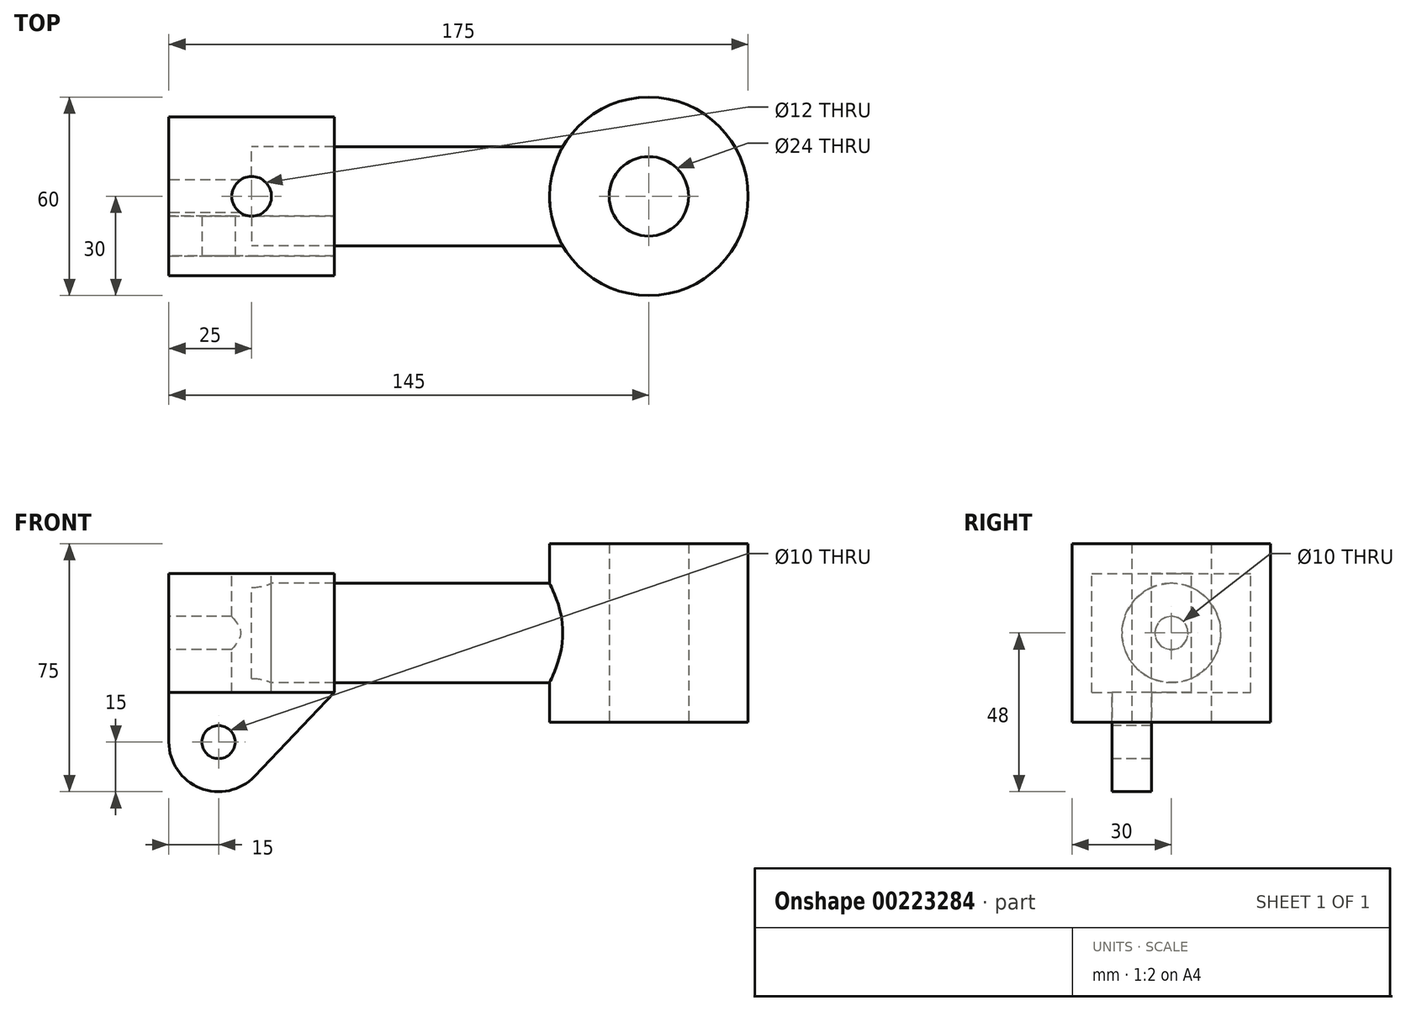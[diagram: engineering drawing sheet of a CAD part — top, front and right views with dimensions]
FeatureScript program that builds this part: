
annotation { "Feature Type Name" : "Feature", "Feature Type Description" : "" }
export const myFeature = defineFeature(function(context is Context, id is Id, definition is map)
    precondition{}
    {
        {
            var Q0;
            Q0=qCreatedBy(makeId("Top.planeOp"),FACE);
            var sketch = newSketch(context, id + "F0", { "sketchPlane" : qUnion([Q0])});
            skCircle(sketch, "E0", {"center": v(0, 0) * mm, "radius": 30 * mm});
            skCircle(sketch, "E1", {"center": v(0, 0) * mm, "radius": 12 * mm});
            skSolve(sketch);
        }
        {
            var Q0;
            Q0=makeQuery(id+"F0.imprint","IMPRINT",FACE,{"disambiguationData":[TD([[makeQuery(id+"F0.imprint","IMPRINT",EDGE,{"derivedFrom":sQuery(id+"F0.wireOp",EDGE,"E0")}),1.0]])]});
            extrude(context, id + "F1", {"entities" : qUnion([Q0]), "depth" : 54 * mm});
        }
        {
            var Q0;
            Q0=qCreatedBy(makeId("Front.planeOp"),FACE);
            var sketch = newSketch(context, id + "F2", { "sketchPlane" : qUnion([Q0])});
            skLineSegment(sketch, "E2.bottom", {"start": v(-95, 9) * mm, "end": v(-145, 9) * mm});
            skLineSegment(sketch, "E2.top", {"start": v(-95, 45) * mm, "end": v(-145, 45) * mm});
            skLineSegment(sketch, "E2.left", {"start": v(-95, 9) * mm, "end": v(-95, 45) * mm});
            skLineSegment(sketch, "E2.right", {"start": v(-145, 9) * mm, "end": v(-145, 45) * mm});
            skPoint(sketch, "E2.middle", {"position": v(-120, 27) * mm});
            skLineSegment(sketch, "E3", {"start": v(-225.9, 0) * mm, "end": v(58.93, 0) * mm, "construction": true});
            skSolve(sketch);
        }
        {
            var Q0;
            Q0=makeQuery(id+"F2.imprint","IMPRINT",FACE,{"disambiguationData":[TD([[makeQuery(id+"F2.imprint","IMPRINT",EDGE,{"derivedFrom":sQuery(id+"F2.wireOp",EDGE,"E2.bottom")}),-1.0]])]});
            extrude(context, id + "F3", {"entities" : qUnion([Q0]), "endBound" : BoundingType.SYMMETRIC, "depth" : 48 * mm});
        }
        {
            var Q0;
            Q0=qCreatedBy(makeId("Top.planeOp"),FACE);
            cPlane(context, id + "F4", {"entities" : qUnion([Q0]), "cplaneType" : CPlaneType.OFFSET, "offset" : 27 * mm, "width" : 150 * mm, "height" : 150 * mm});
        }
        {
            var Q0;
            Q0=qCreatedBy(id+"F4.planeOp",FACE);
            var sketch = newSketch(context, id + "F5", { "sketchPlane" : qUnion([Q0])});
            skLineSegment(sketch, "E4", {"start": v(-120, -40.5) * mm, "end": v(-120, 47.85) * mm, "construction": true});
            skLineSegment(sketch, "E5", {"start": v(0, 0) * mm, "end": v(-120, 0) * mm, "construction": true});
            skSolve(sketch);
        }
        {
            var Q0;
            Q0=qCreatedBy(id+"F4.planeOp",FACE);
            var sketch = newSketch(context, id + "F6", { "sketchPlane" : qUnion([Q0])});
            skLineSegment(sketch, "E6", {"start": v(0, 0) * mm, "end": v(0, -15) * mm});
            skLineSegment(sketch, "E7", {"start": v(0, -15) * mm, "end": v(-120, -15) * mm});
            skLineSegment(sketch, "E8", {"start": v(-120, -15) * mm, "end": v(-120, 0) * mm});
            skLineSegment(sketch, "E9", {"start": v(-120, 0) * mm, "end": v(0, 0) * mm});
            skSolve(sketch);
        }
        {
            var Q0;
            Q0=makeQuery(id+"F6.imprint","IMPRINT",FACE,{"disambiguationData":[TD([[makeQuery(id+"F6.imprint","IMPRINT",EDGE,{"derivedFrom":sQuery(id+"F6.wireOp",EDGE,"E6")}),-1.0]])]});
            var Q1;
            Q1=sQuery(id+"F6.wireOp",EDGE,"E9");
            revolve(context, id + "F7", {"entities" : qUnion([Q0]), "axis" : qUnion([Q1]), "revolveType" : RevolveType.FULL});
        }
        {
            var Q0;
            Q0=makeQuery(id+"F3.opExtrude","SWEPT_FACE",FACE,{"disambiguationData":[OSD([sQuery(id+"F2.wireOp",EDGE,"E2.top")])]});
            var sketch = newSketch(context, id + "F8", { "sketchPlane" : qUnion([Q0])});
            skCircle(sketch, "E10", {"center": v(-120, 0) * mm, "radius": 6 * mm});
            skSolve(sketch);
        }
        {
            var Q0;
            Q0=makeQuery(id+"F8.imprint","IMPRINT",FACE,{"disambiguationData":[TD([[makeQuery(id+"F8.imprint","IMPRINT",EDGE,{"derivedFrom":sQuery(id+"F8.wireOp",EDGE,"E10")}),1.0]])]});
            extrude(context, id + "F9", {"entities" : qUnion([Q0]), "operationType" : NewBodyOperationType.REMOVE, "endBound" : BoundingType.UP_TO_NEXT, "oppositeDirection" : true, "depth" : 25 * mm});
        }
        {
            var Q0;
            Q0=makeQuery(id+"F3.opExtrude","SWEPT_FACE",FACE,{"disambiguationData":[OSD([sQuery(id+"F2.wireOp",EDGE,"E2.right")])]});
            var sketch = newSketch(context, id + "F10", { "sketchPlane" : qUnion([Q0])});
            skCircle(sketch, "E11", {"center": v(0, 27) * mm, "radius": 5 * mm});
            skPoint(sketch, "E11.centerSnap0", {"position": v(-24, 27) * mm});
            skSolve(sketch);
        }
        {
            var Q0;
            Q0=makeQuery(id+"F10.imprint","IMPRINT",FACE,{"disambiguationData":[TD([[makeQuery(id+"F10.imprint","IMPRINT",EDGE,{"derivedFrom":sQuery(id+"F10.wireOp",EDGE,"E11")}),1.0]])]});
            extrude(context, id + "F11", {"entities" : qUnion([Q0]), "operationType" : NewBodyOperationType.REMOVE, "endBound" : BoundingType.UP_TO_NEXT, "oppositeDirection" : true, "depth" : 25 * mm});
        }
        {
            var Q0;
            Q0=makeQuery(id+"F3.opExtrude","CAP_FACE",FACE,{"disambiguationData":[OSD([sQuery(id+"F2.wireOp",EDGE,"E2.bottom"),sQuery(id+"F2.wireOp",EDGE,"E2.top"),sQuery(id+"F2.wireOp",EDGE,"E2.left"),sQuery(id+"F2.wireOp",EDGE,"E2.right")])],"isStart":false});
            cPlane(context, id + "F12", {"entities" : qUnion([Q0]), "cplaneType" : CPlaneType.OFFSET, "offset" : 6 * mm, "oppositeDirection" : true, "width" : 150 * mm, "height" : 150 * mm});
        }
        {
            var Q0;
            Q0=qCreatedBy(id+"F12.planeOp",FACE);
            var sketch = newSketch(context, id + "F13", { "sketchPlane" : qUnion([Q0])});
            skLineSegment(sketch, "E12.0", {"start": v(-95, 9) * mm, "end": v(-145, 9) * mm});
            skLineSegment(sketch, "E13", {"start": v(-145, 9) * mm, "end": v(-145, -6) * mm});
            skLineSegment(sketch, "E14", {"start": v(-119.14, -16.34) * mm, "end": v(-95, 9) * mm});
            skArc(sketch, "E15", {"start": v(-145, -6) * mm, "mid": v(-135.57, -19.93) * mm, "end": v(-119.14, -16.34) * mm});
            skCircle(sketch, "E16", {"center": v(-130, -6) * mm, "radius": 5 * mm});
            skSolve(sketch);
        }
        {
            var Q0;
            Q0=makeQuery(id+"F13.imprint","IMPRINT",FACE,{"disambiguationData":[TD([[makeQuery(id+"F13.imprint","IMPRINT",EDGE,{"derivedFrom":sQuery(id+"F13.wireOp",EDGE,"E12.0")}),1.0]])]});
            extrude(context, id + "F14", {"entities" : qUnion([Q0]), "operationType" : NewBodyOperationType.ADD, "oppositeDirection" : true, "depth" : 12 * mm});
        }
        {
            var Q0;
            Q0=makeQuery(id+"F1.opExtrude","SWEPT_BODY",BODY,{"disambiguationData":[OSD([sQuery(id+"F0.wireOp",EDGE,"E0"),sQuery(id+"F0.wireOp",EDGE,"E1")])]});
            var Q1;
            Q1=qCreatedBy(makeId("Front.planeOp"),FACE);
            mirror(context, id + "F15", {"operationType" : NewBodyOperationType.ADD, "entities" : qUnion([Q0]), "mirrorPlane" : qUnion([Q1])});
        }
        {
            var Q0;
            Q0=makeQuery(id+"F1.opExtrude","CAP_FACE",FACE,{"disambiguationData":[OSD([sQuery(id+"F0.wireOp",EDGE,"E0"),sQuery(id+"F0.wireOp",EDGE,"E1")])],"isStart":false});
            var sketch = newSketch(context, id + "F16", { "sketchPlane" : qUnion([Q0])});
            skCircle(sketch, "E17.0", {"center": v(0, 0) * mm, "radius": 12 * mm});
            skSolve(sketch);
        }
        {
            var Q0;
            Q0 = qSketchRegion(id + "F16", true);
            extrude(context, id + "F17", {"entities" : qUnion([Q0]), "operationType" : NewBodyOperationType.REMOVE, "endBound" : BoundingType.THROUGH_ALL, "oppositeDirection" : true, "depth" : 25 * mm});
        }
    });
